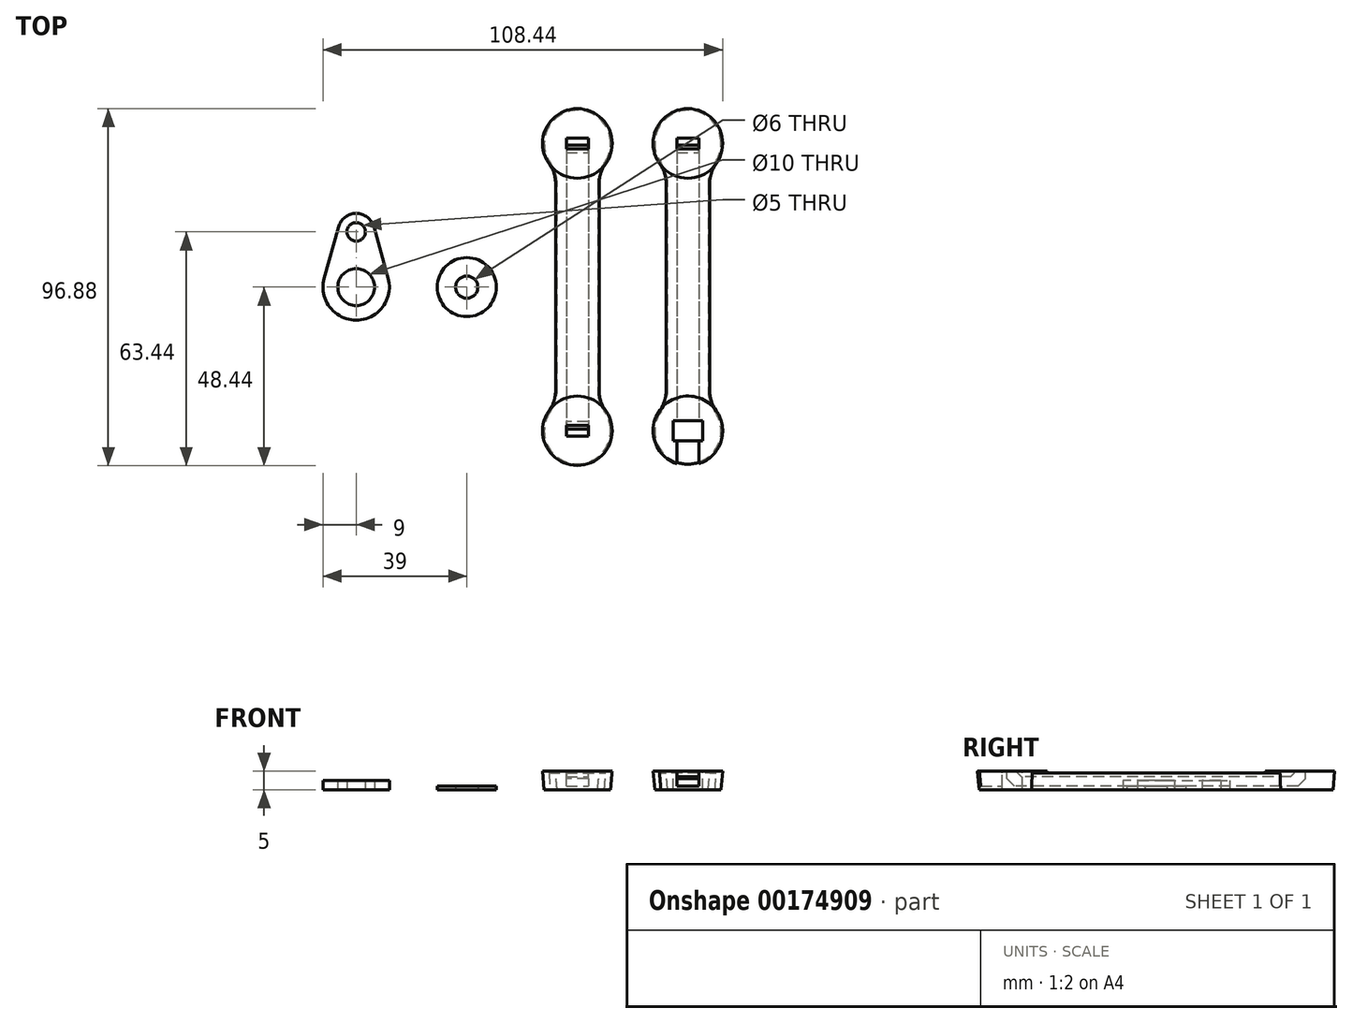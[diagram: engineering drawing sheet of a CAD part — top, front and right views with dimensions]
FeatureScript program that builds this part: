
annotation { "Feature Type Name" : "Feature", "Feature Type Description" : "" }
export const myFeature = defineFeature(function(context is Context, id is Id, definition is map)
    precondition{}
    {
        {
            var Q0;
            Q0=qCreatedBy(makeId("Top.planeOp"),FACE);
            var sketch = newSketch(context, id + "F0", { "sketchPlane" : qUnion([Q0])});
            skLineSegment(sketch, "E0.bottom", {"start": v(5.5, 39) * mm, "end": v(-5.5, 39) * mm});
            skLineSegment(sketch, "E0.top", {"start": v(5.5, -39) * mm, "end": v(-5.5, -39) * mm});
            skLineSegment(sketch, "E0.left", {"start": v(5.5, 39) * mm, "end": v(5.5, -39) * mm});
            skLineSegment(sketch, "E0.right", {"start": v(-5.5, 39) * mm, "end": v(-5.5, -39) * mm});
            skPoint(sketch, "E0.middle", {"position": v(0, 0) * mm});
            skSolve(sketch);
        }
        {
            var Q0;
            Q0 = qSketchRegion(id + "F0", true);
            extrude(context, id + "F1", {"entities" : qUnion([Q0]), "depth" : 4.5 * mm, "hasDraft" : true, "draftAngle" : 5 * degree});
        }
        {
            var Q0;
            Q0=qCreatedBy(makeId("Front.planeOp"),FACE);
            var sketch = newSketch(context, id + "F2", { "sketchPlane" : qUnion([Q0])});
            skLineSegment(sketch, "E1.bottom", {"start": v(3, 1) * mm, "end": v(-3, 1) * mm});
            skLineSegment(sketch, "E1.top", {"start": v(3, 3.5) * mm, "end": v(-3, 3.5) * mm});
            skLineSegment(sketch, "E1.left", {"start": v(3, 1) * mm, "end": v(3, 3.5) * mm});
            skLineSegment(sketch, "E1.right", {"start": v(-3, 1) * mm, "end": v(-3, 3.5) * mm});
            skPoint(sketch, "E1.middle", {"position": v(0, 2.25) * mm});
            skSolve(sketch);
        }
        {
            var Q0;
            Q0=qCreatedBy(makeId("Top.planeOp"),FACE);
            var sketch = newSketch(context, id + "F3", { "sketchPlane" : qUnion([Q0])});
            skCircle(sketch, "E2", {"center": v(0, -39) * mm, "radius": 9 * mm});
            skLineSegment(sketch, "E3", {"start": v(0, 0) * mm, "end": v(18.48, 0) * mm, "construction": true});
            skCircle(sketch, "E4.MirrorC", {"center": v(0, 39) * mm, "radius": 9 * mm});
            skSolve(sketch);
        }
        {
            var Q0;
            Q0 = qSketchRegion(id + "F3", true);
            extrude(context, id + "F4", {"entities" : qUnion([Q0]), "operationType" : NewBodyOperationType.ADD, "depth" : 5 * mm, "hasDraft" : true, "draftAngle" : 5 * degree});
        }
        {
            var Q0;
            Q0 = qSketchRegion(id + "F2", true);
            extrude(context, id + "F5", {"entities" : qUnion([Q0]), "operationType" : NewBodyOperationType.REMOVE, "oppositeDirection" : true, "depth" : 40 * mm, "hasSecondDirection" : true, "secondDirectionOppositeDirection" : false, "secondDirectionDepth" : 40 * mm});
        }
        {
            var Q0;
            Q0=makeQuery(id+"F4.opExtrude","CAP_FACE",FACE,{"disambiguationData":[OSD([sQuery(id+"F3.wireOp",EDGE,"E2")])],"isStart":false});
            var sketch = newSketch(context, id + "F6", { "sketchPlane" : qUnion([Q0])});
            skLineSegment(sketch, "E5.bottom", {"start": v(3, -37.5) * mm, "end": v(-3, -37.5) * mm});
            skLineSegment(sketch, "E5.top", {"start": v(3, -40.5) * mm, "end": v(-3, -40.5) * mm});
            skLineSegment(sketch, "E5.left", {"start": v(3, -37.5) * mm, "end": v(3, -40.5) * mm});
            skLineSegment(sketch, "E5.right", {"start": v(-3, -37.5) * mm, "end": v(-3, -40.5) * mm});
            skPoint(sketch, "E5.middle", {"position": v(0, -39) * mm});
            skLineSegment(sketch, "E6", {"start": v(0, 0) * mm, "end": v(15.24, 0) * mm, "construction": true});
            skLineSegment(sketch, "E7.MirrorCS", {"start": v(3, 37.5) * mm, "end": v(3, 40.5) * mm});
            skLineSegment(sketch, "E8.MirrorCS", {"start": v(-3, 37.5) * mm, "end": v(-3, 40.5) * mm});
            skPoint(sketch, "E9.MirrorP", {"position": v(0, 39) * mm});
            skLineSegment(sketch, "E10.MirrorCS", {"start": v(3, 37.5) * mm, "end": v(-3, 37.5) * mm});
            skLineSegment(sketch, "E11.MirrorCS", {"start": v(3, 40.5) * mm, "end": v(-3, 40.5) * mm});
            skSolve(sketch);
        }
        {
            var Q0;
            Q0 = qSketchRegion(id + "F6", true);
            var Q1;
            Q1=makeQuery(id+"F5.boolean.opBoolean","COPY",FACE,{"derivedFrom":makeQuery(id+"F5.opExtrude","SWEPT_FACE",FACE,{"disambiguationData":[OSD([sQuery(id+"F2.wireOp",EDGE,"E1.bottom")])]})});
            extrude(context, id + "F7", {"entities" : qUnion([Q0]), "operationType" : NewBodyOperationType.REMOVE, "endBound" : BoundingType.UP_TO_SURFACE, "oppositeDirection" : true, "endBoundEntityFace" : qUnion([Q1]), "depth" : 25 * mm});
        }
        {
            var Q0;
            Q0=makeQuery(id+"F7.boolean.opBoolean","COPY",EDGE,{"derivedFrom":makeQuery(id+"F7.opExtrude","CAP_EDGE",EDGE,{"disambiguationData":[OSD([sQuery(id+"F6.wireOp",EDGE,"E5.top")])],"isStart":false})});
            var Q1;
            Q1=makeQuery(id+"F7.boolean.opBoolean","COPY",EDGE,{"derivedFrom":makeQuery(id+"F7.opExtrude","CAP_EDGE",EDGE,{"disambiguationData":[OSD([sQuery(id+"F6.wireOp",EDGE,"E11.MirrorCS")])],"isStart":false})});
            chamfer(context, id + "F8", {"entities" : qUnion([Q0, Q1]), "width" : 2 * mm, "tangentPropagation" : true});
        }
        {
            var Q0;
            Q0=makeQuery(id+"F7.boolean.opBoolean","INTERSECT",EDGE,{"derivedFrom":[makeQuery(id+"F5.boolean.opBoolean","COPY",FACE,{"derivedFrom":makeQuery(id+"F5.opExtrude","SWEPT_FACE",FACE,{"disambiguationData":[OSD([sQuery(id+"F2.wireOp",EDGE,"E1.top")])]})}),makeQuery(id+"F7.opExtrude","SWEPT_FACE",FACE,{"disambiguationData":[OSD([sQuery(id+"F6.wireOp",EDGE,"E10.MirrorCS")])]})]});
            var Q1;
            Q1=makeQuery(id+"F7.boolean.opBoolean","INTERSECT",EDGE,{"derivedFrom":[makeQuery(id+"F5.boolean.opBoolean","COPY",FACE,{"derivedFrom":makeQuery(id+"F5.opExtrude","SWEPT_FACE",FACE,{"disambiguationData":[OSD([sQuery(id+"F2.wireOp",EDGE,"E1.top")])]})}),makeQuery(id+"F7.opExtrude","SWEPT_FACE",FACE,{"disambiguationData":[OSD([sQuery(id+"F6.wireOp",EDGE,"E5.bottom")])]})]});
            chamfer(context, id + "F9", {"entities" : qUnion([Q0, Q1]), "width" : 1 * mm, "tangentPropagation" : true});
        }
        {
            var Q0;
            Q0=makeQuery(id+"F1.opExtrude","SWEPT_BODY",BODY,{"disambiguationData":[OSD([sQuery(id+"F0.wireOp",EDGE,"E0.bottom"),sQuery(id+"F0.wireOp",EDGE,"E0.top"),sQuery(id+"F0.wireOp",EDGE,"E0.left"),sQuery(id+"F0.wireOp",EDGE,"E0.right")])]});
            transform(context, id + "F10", {"entities" : qUnion([Q0]), "transformType" : TransformType.TRANSLATION_3D, "dx" : 30 * mm, "dy" : 0 * mm, "dz" : 0 * mm, "makeCopy" : true});
        }
        {
            var Q0;
            Q0=makeQuery(id+"F4.opExtrude","CAP_FACE",FACE,{"disambiguationData":[OSD([sQuery(id+"F3.wireOp",EDGE,"E2")])],"isStart":false});
            var sketch = newSketch(context, id + "F11", { "sketchPlane" : qUnion([Q0])});
            skLineSegment(sketch, "E12.bottom", {"start": v(4, -36.25) * mm, "end": v(-4, -36.25) * mm});
            skLineSegment(sketch, "E12.top", {"start": v(4, -41.75) * mm, "end": v(-4, -41.75) * mm});
            skLineSegment(sketch, "E12.left", {"start": v(4, -36.25) * mm, "end": v(4, -41.75) * mm});
            skLineSegment(sketch, "E12.right", {"start": v(-4, -36.25) * mm, "end": v(-4, -41.75) * mm});
            skPoint(sketch, "E12.middle", {"position": v(0, -39) * mm});
            skLineSegment(sketch, "E13", {"start": v(0, -39) * mm, "end": v(3, -39) * mm, "construction": true});
            skSolve(sketch);
        }
        {
            var Q0;
            Q0 = qSketchRegion(id + "F11", true);
            extrude(context, id + "F12", {"entities" : qUnion([Q0]), "operationType" : NewBodyOperationType.REMOVE, "endBound" : BoundingType.THROUGH_ALL, "oppositeDirection" : true, "depth" : 25 * mm});
        }
        {
            var Q0;
            Q0=makeQuery(id+"F12.boolean.opBoolean","COPY",FACE,{"derivedFrom":makeQuery(id+"F12.opExtrude","SWEPT_FACE",FACE,{"disambiguationData":[OSD([sQuery(id+"F11.wireOp",EDGE,"E12.bottom")])]})});
            var sketch = newSketch(context, id + "F13", { "sketchPlane" : qUnion([Q0])});
            skLineSegment(sketch, "E14.0", {"start": v(3, 1) * mm, "end": v(-3, 1) * mm});
            skLineSegment(sketch, "E14.1", {"start": v(3, 1) * mm, "end": v(3, 3.5) * mm});
            skLineSegment(sketch, "E14.3", {"start": v(-3, 1) * mm, "end": v(-3, 3.5) * mm});
            skLineSegment(sketch, "E15", {"start": v(3, 3.5) * mm, "end": v(3, 5) * mm});
            skLineSegment(sketch, "E16", {"start": v(3, 5) * mm, "end": v(-3, 5) * mm});
            skLineSegment(sketch, "E17", {"start": v(-3, 5) * mm, "end": v(-3, 3.5) * mm});
            skSolve(sketch);
        }
        {
            var Q0;
            Q0 = qSketchRegion(id + "F13", true);
            extrude(context, id + "F14", {"entities" : qUnion([Q0]), "operationType" : NewBodyOperationType.REMOVE, "endBound" : BoundingType.THROUGH_ALL, "depth" : 25 * mm});
        }
        {
            var Q0;
            Q0=makeQuery(id+"F1.opExtrude","SWEPT_BODY",BODY,{"disambiguationData":[OSD([sQuery(id+"F0.wireOp",EDGE,"E0.bottom"),sQuery(id+"F0.wireOp",EDGE,"E0.top"),sQuery(id+"F0.wireOp",EDGE,"E0.left"),sQuery(id+"F0.wireOp",EDGE,"E0.right")])]});
            transform(context, id + "F15", {"entities" : qUnion([Q0]), "transformType" : TransformType.TRANSLATION_3D, "dx" : 60 * mm, "dy" : 0 * mm, "dz" : 0 * mm, "makeCopy" : false});
        }
        {
            var Q0;
            Q0=qCreatedBy(makeId("Top.planeOp"),FACE);
            var sketch = newSketch(context, id + "F16", { "sketchPlane" : qUnion([Q0])});
            skCircle(sketch, "E18", {"center": v(0, 0) * mm, "radius": 5 * mm});
            skArc(sketch, "E19", {"start": v(-8.67, 2.4) * mm, "mid": v(0, -9) * mm, "end": v(8.67, 2.4) * mm});
            skLineSegment(sketch, "E20.left", {"start": v(4.82, 16.33) * mm, "end": v(8.67, 2.4) * mm});
            skCircle(sketch, "E21", {"center": v(0, 15) * mm, "radius": 2.5 * mm});
            skArc(sketch, "E22", {"start": v(4.82, 16.33) * mm, "mid": v(0, 20) * mm, "end": v(-4.82, 16.33) * mm});
            skLineSegment(sketch, "E23", {"start": v(-8.67, 2.4) * mm, "end": v(-4.82, 16.33) * mm});
            skSolve(sketch);
        }
        {
            var Q0;
            Q0 = qSketchRegion(id + "F16", true);
            extrude(context, id + "F17", {"entities" : qUnion([Q0]), "depth" : 2.5 * mm});
        }
        {
            var Q0;
            Q0=makeQuery(id+"F17.opExtrude","SWEPT_BODY",BODY,{"disambiguationData":[OSD([sQuery(id+"F16.wireOp",EDGE,"E18"),sQuery(id+"F16.wireOp",EDGE,"E19"),sQuery(id+"F16.wireOp",EDGE,"E20.left"),sQuery(id+"F16.wireOp",EDGE,"E21"),sQuery(id+"F16.wireOp",EDGE,"E22"),sQuery(id+"F16.wireOp",EDGE,"E23")])]});
            transform(context, id + "F18", {"entities" : qUnion([Q0]), "transformType" : TransformType.TRANSLATION_3D, "dx" : -30 * mm, "dy" : 0 * mm, "dz" : 0 * mm, "makeCopy" : false});
        }
        {
            var Q0;
            Q0=qCreatedBy(makeId("Top.planeOp"),FACE);
            var sketch = newSketch(context, id + "F19", { "sketchPlane" : qUnion([Q0])});
            skCircle(sketch, "E24", {"center": v(0, 0) * mm, "radius": 3 * mm});
            skCircle(sketch, "E25", {"center": v(0, 0) * mm, "radius": 8 * mm});
            skSolve(sketch);
        }
        {
            var Q0;
            Q0 = qSketchRegion(id + "F19", true);
            extrude(context, id + "F20", {"entities" : qUnion([Q0]), "depth" : 1 * mm});
        }
        {
            var Q0;
            Q0=makeQuery(id+"F4.boolean.opBoolean","INTERSECT",EDGE,{"derivedFrom":[makeQuery(id+"F1.opExtrude","SWEPT_FACE",FACE,{"disambiguationData":[OSD([sQuery(id+"F0.wireOp",EDGE,"E0.left")])]}),makeQuery(id+"F4.opExtrude","SWEPT_FACE",FACE,{"disambiguationData":[OSD([sQuery(id+"F3.wireOp",EDGE,"E2")])]})]});
            var Q1;
            Q1=makeQuery(id+"F4.boolean.opBoolean","INTERSECT",EDGE,{"derivedFrom":[makeQuery(id+"F1.opExtrude","SWEPT_FACE",FACE,{"disambiguationData":[OSD([sQuery(id+"F0.wireOp",EDGE,"E0.left")])]}),makeQuery(id+"F4.opExtrude","SWEPT_FACE",FACE,{"disambiguationData":[OSD([sQuery(id+"F3.wireOp",EDGE,"E4.MirrorC")])]})]});
            var Q2;
            Q2=makeQuery(id+"F10.opPattern","COPY",EDGE,{"derivedFrom":makeQuery(id+"F4.boolean.opBoolean","INTERSECT",EDGE,{"derivedFrom":[makeQuery(id+"F1.opExtrude","SWEPT_FACE",FACE,{"disambiguationData":[OSD([sQuery(id+"F0.wireOp",EDGE,"E0.left")])]}),makeQuery(id+"F4.opExtrude","SWEPT_FACE",FACE,{"disambiguationData":[OSD([sQuery(id+"F3.wireOp",EDGE,"E2")])]})]}),"instanceName":"1"});
            var Q3;
            Q3=makeQuery(id+"F10.opPattern","COPY",EDGE,{"derivedFrom":makeQuery(id+"F4.boolean.opBoolean","INTERSECT",EDGE,{"derivedFrom":[makeQuery(id+"F1.opExtrude","SWEPT_FACE",FACE,{"disambiguationData":[OSD([sQuery(id+"F0.wireOp",EDGE,"E0.left")])]}),makeQuery(id+"F4.opExtrude","SWEPT_FACE",FACE,{"disambiguationData":[OSD([sQuery(id+"F3.wireOp",EDGE,"E4.MirrorC")])]})]}),"instanceName":"1"});
            var Q4;
            Q4=makeQuery(id+"F4.boolean.opBoolean","INTERSECT",EDGE,{"derivedFrom":[makeQuery(id+"F1.opExtrude","SWEPT_FACE",FACE,{"disambiguationData":[OSD([sQuery(id+"F0.wireOp",EDGE,"E0.right")])]}),makeQuery(id+"F4.opExtrude","SWEPT_FACE",FACE,{"disambiguationData":[OSD([sQuery(id+"F3.wireOp",EDGE,"E4.MirrorC")])]})]});
            var Q5;
            Q5=makeQuery(id+"F10.opPattern","COPY",EDGE,{"derivedFrom":makeQuery(id+"F4.boolean.opBoolean","INTERSECT",EDGE,{"derivedFrom":[makeQuery(id+"F1.opExtrude","SWEPT_FACE",FACE,{"disambiguationData":[OSD([sQuery(id+"F0.wireOp",EDGE,"E0.right")])]}),makeQuery(id+"F4.opExtrude","SWEPT_FACE",FACE,{"disambiguationData":[OSD([sQuery(id+"F3.wireOp",EDGE,"E4.MirrorC")])]})]}),"instanceName":"1"});
            var Q6;
            Q6=makeQuery(id+"F10.opPattern","COPY",EDGE,{"derivedFrom":makeQuery(id+"F4.boolean.opBoolean","INTERSECT",EDGE,{"derivedFrom":[makeQuery(id+"F1.opExtrude","SWEPT_FACE",FACE,{"disambiguationData":[OSD([sQuery(id+"F0.wireOp",EDGE,"E0.right")])]}),makeQuery(id+"F4.opExtrude","SWEPT_FACE",FACE,{"disambiguationData":[OSD([sQuery(id+"F3.wireOp",EDGE,"E2")])]})]}),"instanceName":"1"});
            var Q7;
            Q7=makeQuery(id+"F4.boolean.opBoolean","INTERSECT",EDGE,{"derivedFrom":[makeQuery(id+"F1.opExtrude","SWEPT_FACE",FACE,{"disambiguationData":[OSD([sQuery(id+"F0.wireOp",EDGE,"E0.right")])]}),makeQuery(id+"F4.opExtrude","SWEPT_FACE",FACE,{"disambiguationData":[OSD([sQuery(id+"F3.wireOp",EDGE,"E2")])]})]});
            fillet(context, id + "F21", {"entities" : qUnion([Q0, Q1, Q2, Q3, Q4, Q5, Q6, Q7]), "radius" : 10 * mm, "tangentPropagation" : true, "allowEdgeOverflow" : false});
        }
    });
